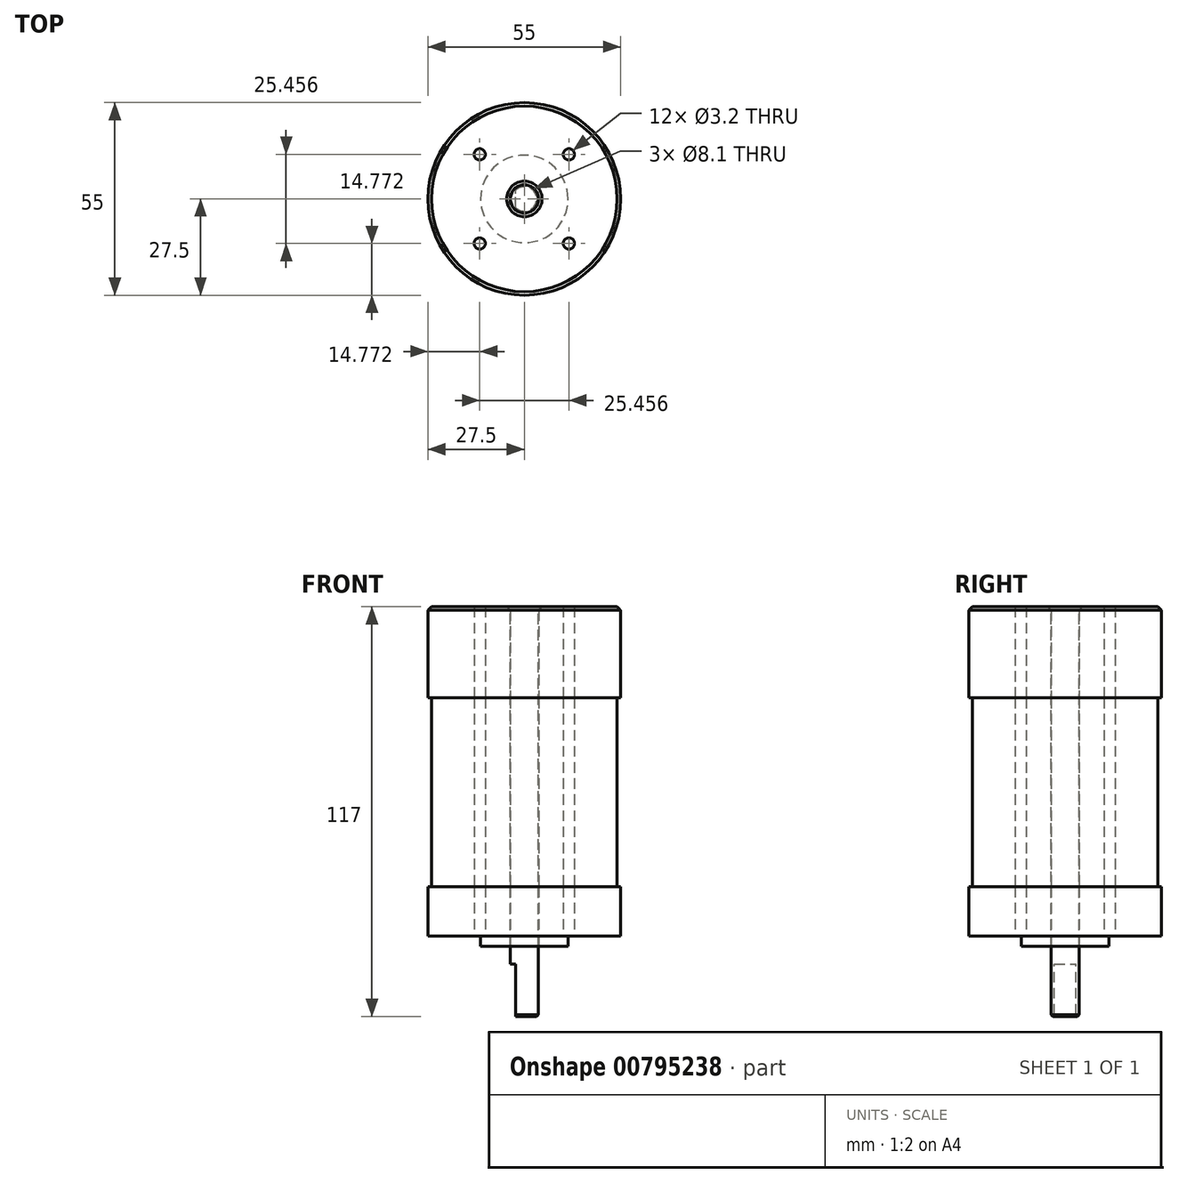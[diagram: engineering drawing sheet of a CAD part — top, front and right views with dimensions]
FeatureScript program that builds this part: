
annotation { "Feature Type Name" : "Feature", "Feature Type Description" : "" }
export const myFeature = defineFeature(function(context is Context, id is Id, definition is map)
    precondition{}
    {
        {
            var Q0;
            Q0=qCreatedBy(makeId("Top.planeOp"),FACE);
            var sketch = newSketch(context, id + "F0", { "sketchPlane" : qUnion([Q0])});
            skCircle(sketch, "E0", {"center": v(0, 0) * mm, "radius": 27.5 * mm});
            skSolve(sketch);
        }
        {
            var Q0;
            Q0=makeQuery(id+"F0.imprint","IMPRINT",FACE,{"disambiguationData":[TD([[makeQuery(id+"F0.imprint","IMPRINT",EDGE,{"derivedFrom":sQuery(id+"F0.wireOp",EDGE,"E0")}),1.0]])]});
            extrude(context, id + "F1", {"entities" : qUnion([Q0]), "depth" : 17 * mm, "offsetDistance" : 25 * mm});
        }
        {
            var Q0;
            Q0=makeQuery(id+"F1.opExtrude","CAP_FACE",FACE,{"disambiguationData":[OSD([sQuery(id+"F0.wireOp",EDGE,"E0")])],"isStart":true});
            var sketch = newSketch(context, id + "F2", { "sketchPlane" : qUnion([Q0])});
            skCircle(sketch, "E1", {"center": v(0, 0) * mm, "radius": 12.5 * mm});
            skSolve(sketch);
        }
        {
            var Q0;
            Q0=makeQuery(id+"F2.imprint","IMPRINT",FACE,{"disambiguationData":[TD([[makeQuery(id+"F2.imprint","IMPRINT",EDGE,{"derivedFrom":sQuery(id+"F2.wireOp",EDGE,"E1")}),-1.0]])]});
            extrude(context, id + "F3", {"entities" : qUnion([Q0]), "operationType" : NewBodyOperationType.REMOVE, "oppositeDirection" : true, "depth" : 3 * mm, "offsetDistance" : 25 * mm});
        }
        {
            var Q0;
            Q0=makeQuery(id+"F1.opExtrude","CAP_FACE",FACE,{"disambiguationData":[OSD([sQuery(id+"F0.wireOp",EDGE,"E0")])],"isStart":false});
            var sketch = newSketch(context, id + "F4", { "sketchPlane" : qUnion([Q0])});
            skCircle(sketch, "E2", {"center": v(0, 0) * mm, "radius": 26.5 * mm});
            skSolve(sketch);
        }
        {
            var Q0;
            Q0=makeQuery(id+"F4.imprint","IMPRINT",FACE,{"disambiguationData":[TD([[makeQuery(id+"F4.imprint","IMPRINT",EDGE,{"derivedFrom":sQuery(id+"F4.wireOp",EDGE,"E2")}),1.0]])]});
            extrude(context, id + "F5", {"entities" : qUnion([Q0]), "depth" : 54 * mm, "offsetDistance" : 25 * mm});
        }
        {
            var Q0;
            Q0=makeQuery(id+"F5.opExtrude","CAP_FACE",FACE,{"disambiguationData":[OSD([sQuery(id+"F4.wireOp",EDGE,"E2")])],"isStart":false});
            var sketch = newSketch(context, id + "F6", { "sketchPlane" : qUnion([Q0])});
            skCircle(sketch, "E3", {"center": v(0, 0) * mm, "radius": 27.5 * mm});
            skSolve(sketch);
        }
        {
            var Q0;
            Q0 = qSketchRegion(id + "F6", true);
            extrude(context, id + "F7", {"entities" : qUnion([Q0]), "depth" : 26 * mm, "offsetDistance" : 25 * mm});
        }
        {
            var Q0;
            Q0=makeQuery(id+"F7.opExtrude","CAP_EDGE",EDGE,{"disambiguationData":[OSD([sQuery(id+"F6.wireOp",EDGE,"E3")])],"isStart":false});
            var Q1;
            Q1=makeQuery(id+"F3.boolean.opBoolean","COPY",EDGE,{"derivedFrom":makeQuery(id+"F3.opExtrude","CAP_EDGE",EDGE,{"disambiguationData":[OSD([sQuery(id+"F0.wireOp",EDGE,"E0")])],"isStart":false})});
            chamfer(context, id + "F8", {"entities" : qUnion([Q0, Q1]), "width" : 1 * mm, "tangentPropagation" : true});
        }
        {
            var Q0;
            Q0=makeQuery(id+"F1.opExtrude","CAP_FACE",FACE,{"disambiguationData":[OSD([sQuery(id+"F0.wireOp",EDGE,"E0")])],"isStart":true});
            var sketch = newSketch(context, id + "F9", { "sketchPlane" : qUnion([Q0])});
            skCircle(sketch, "E4", {"center": v(0, 0) * mm, "radius": 4.05 * mm});
            skSolve(sketch);
        }
        {
            var Q0;
            Q0=makeQuery(id+"F9.imprint","IMPRINT",FACE,{"disambiguationData":[TD([[makeQuery(id+"F9.imprint","IMPRINT",EDGE,{"derivedFrom":sQuery(id+"F9.wireOp",EDGE,"E4")}),1.0]])]});
            extrude(context, id + "F10", {"entities" : qUnion([Q0]), "operationType" : NewBodyOperationType.REMOVE, "endBound" : BoundingType.THROUGH_ALL, "oppositeDirection" : true, "depth" : 25 * mm, "offsetDistance" : 25 * mm});
        }
        {
            var Q0;
            Q0=makeQuery(id+"F10.boolean.opBoolean","INTERSECT",EDGE,{"derivedFrom":[makeQuery(id+"F7.opExtrude","CAP_FACE",FACE,{"disambiguationData":[OSD([sQuery(id+"F6.wireOp",EDGE,"E3")])],"isStart":false}),makeQuery(id+"F10.opExtrude","SWEPT_FACE",FACE,{"disambiguationData":[OSD([sQuery(id+"F9.wireOp",EDGE,"E4")])]})]});
            var Q1;
            Q1=makeQuery(id+"F10.boolean.opBoolean","COPY",EDGE,{"derivedFrom":makeQuery(id+"F10.opExtrude","CAP_EDGE",EDGE,{"disambiguationData":[OSD([sQuery(id+"F9.wireOp",EDGE,"E4")])],"isStart":true})});
            chamfer(context, id + "F11", {"entities" : qUnion([Q0, Q1]), "width" : 1 * mm, "tangentPropagation" : true});
        }
        {
            var Q0;
            Q0=makeQuery(id+"F7.opExtrude","CAP_FACE",FACE,{"disambiguationData":[OSD([sQuery(id+"F6.wireOp",EDGE,"E3")])],"isStart":false});
            var sketch = newSketch(context, id + "F12", { "sketchPlane" : qUnion([Q0])});
            skCircle(sketch, "E5", {"center": v(0, 0) * mm, "radius": 4 * mm});
            skSolve(sketch);
        }
        {
            var Q0;
            Q0 = qSketchRegion(id + "F12", true);
            extrude(context, id + "F13", {"entities" : qUnion([Q0]), "oppositeDirection" : true, "depth" : 117 * mm, "offsetDistance" : 25 * mm});
        }
        {
            var Q0;
            Q0=makeQuery(id+"F13.opExtrude","CAP_EDGE",EDGE,{"disambiguationData":[OSD([sQuery(id+"F12.wireOp",EDGE,"E5")])],"isStart":false});
            chamfer(context, id + "F14", {"entities" : qUnion([Q0]), "width" : .5 * mm, "tangentPropagation" : true});
        }
        {
            var Q0;
            Q0=makeQuery(id+"F13.opExtrude","CAP_FACE",FACE,{"disambiguationData":[OSD([sQuery(id+"F12.wireOp",EDGE,"E5")])],"isStart":false});
            var sketch = newSketch(context, id + "F15", { "sketchPlane" : qUnion([Q0])});
            skArc(sketch, "E6", {"start": v(-2.5, 6.51) * mm, "mid": v(-6.98, 0) * mm, "end": v(-2.5, -6.51) * mm});
            skLineSegment(sketch, "E7", {"start": v(-2.5, 6.51) * mm, "end": v(-2.5, -6.51) * mm});
            skSolve(sketch);
        }
        {
            var Q0;
            Q0 = qSketchRegion(id + "F15", true);
            extrude(context, id + "F16", {"entities" : qUnion([Q0]), "operationType" : NewBodyOperationType.REMOVE, "oppositeDirection" : true, "depth" : 15 * mm, "offsetDistance" : 25 * mm});
        }
        {
            var Q0;
            Q0=makeQuery(id+"F3.boolean.opBoolean","COPY",FACE,{"derivedFrom":makeQuery(id+"F3.opExtrude","CAP_FACE",FACE,{"disambiguationData":[OSD([sQuery(id+"F0.wireOp",EDGE,"E0"),sQuery(id+"F2.wireOp",EDGE,"E1")])],"isStart":false})});
            var sketch = newSketch(context, id + "F17", { "sketchPlane" : qUnion([Q0])});
            skCircle(sketch, "E8", {"center": v(0, 0) * mm, "radius": 18 * mm, "construction": true});
            skLineSegment(sketch, "E9", {"start": v(0, 0) * mm, "end": v(-26.42, 26.42) * mm, "construction": true});
            skCircle(sketch, "E10", {"center": v(-12.73, 12.73) * mm, "radius": 1.6 * mm});
            skCircle(sketch, "E11.1.0", {"center": v(-12.73, -12.73) * mm, "radius": 1.6 * mm});
            skCircle(sketch, "E11.2.0", {"center": v(12.73, -12.73) * mm, "radius": 1.6 * mm});
            skCircle(sketch, "E11.3.0", {"center": v(12.73, 12.73) * mm, "radius": 1.6 * mm});
            skSolve(sketch);
        }
        {
            var Q0;
            Q0 = qSketchRegion(id + "F17", true);
            extrude(context, id + "F18", {"entities" : qUnion([Q0]), "operationType" : NewBodyOperationType.REMOVE, "endBound" : BoundingType.THROUGH_ALL, "oppositeDirection" : true, "depth" : 25 * mm, "offsetDistance" : 25 * mm});
        }
    });
